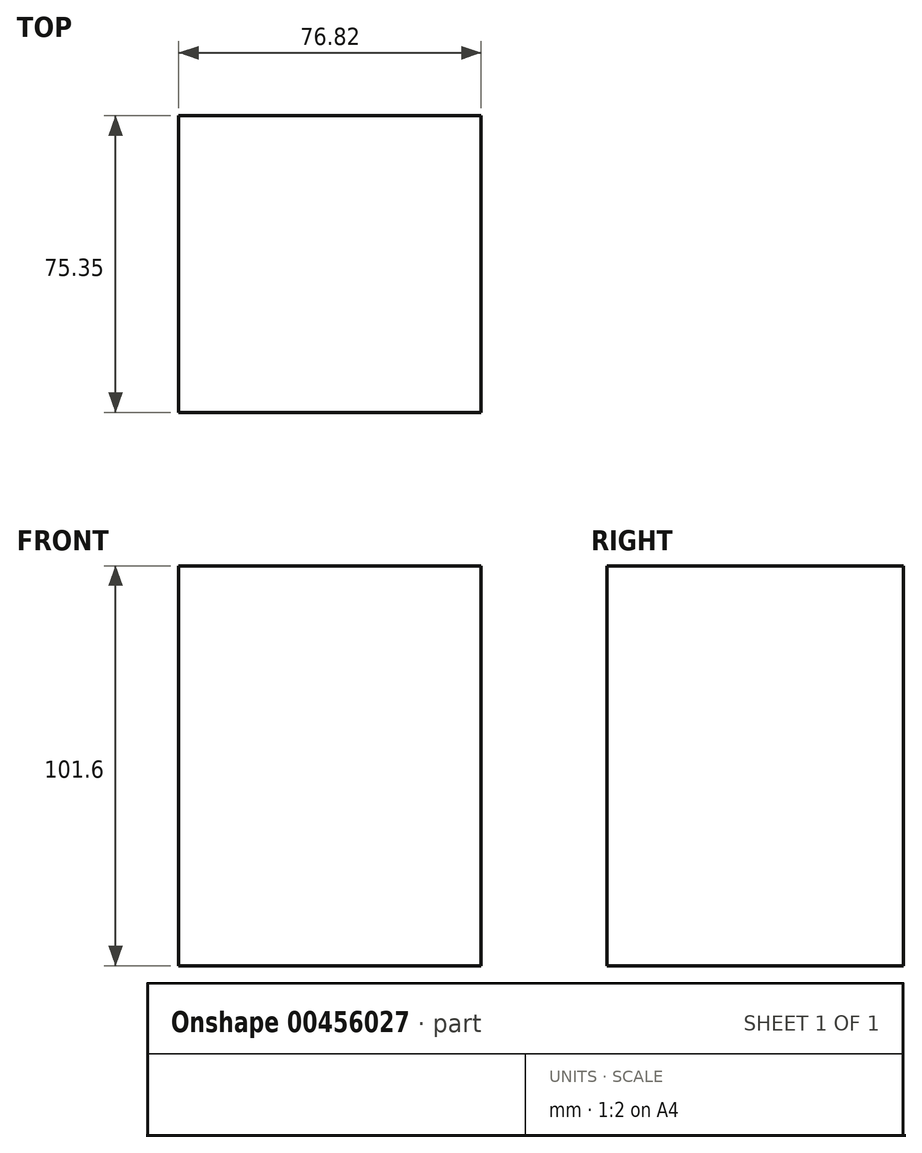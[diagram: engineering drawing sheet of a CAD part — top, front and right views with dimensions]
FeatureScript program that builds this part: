
annotation { "Feature Type Name" : "Feature", "Feature Type Description" : "" }
export const myFeature = defineFeature(function(context is Context, id is Id, definition is map)
    precondition{}
    {
        {
            var Q0;
            Q0=qCreatedBy(makeId("Top.planeOp"),FACE);
            var sketch = newSketch(context, id + "F0", { "sketchPlane" : qUnion([Q0])});
            skLineSegment(sketch, "E0.bottom", {"start": v(0, 0) * mm, "end": v(76.82, 0) * mm});
            skLineSegment(sketch, "E0.top", {"start": v(0, 75.35) * mm, "end": v(76.82, 75.35) * mm});
            skLineSegment(sketch, "E0.left", {"start": v(0, 0) * mm, "end": v(0, 75.35) * mm});
            skLineSegment(sketch, "E0.right", {"start": v(76.82, 0) * mm, "end": v(76.82, 75.35) * mm});
            skSolve(sketch);
        }
        {
            var Q0;
            Q0=makeQuery(id+"F0.imprint","IMPRINT",FACE,{"disambiguationData":[TD([[makeQuery(id+"F0.imprint","IMPRINT",EDGE,{"derivedFrom":sQuery(id+"F0.wireOp",EDGE,"E0.bottom")}),1.0]])]});
            var sketch = newSketch(context, id + "F1", { "sketchPlane" : qUnion([Q0])});
            skLineSegment(sketch, "E1.bottom", {"start": v(39.55, 39.24) * mm, "end": v(75.99, 39.24) * mm});
            skLineSegment(sketch, "E1.top", {"start": v(39.55, 74.91) * mm, "end": v(75.99, 74.91) * mm});
            skLineSegment(sketch, "E1.left", {"start": v(39.55, 39.24) * mm, "end": v(39.55, 74.91) * mm});
            skLineSegment(sketch, "E1.right", {"start": v(75.99, 39.24) * mm, "end": v(75.99, 74.91) * mm});
            skLineSegment(sketch, "E2.top", {"start": v(39.55, 0) * mm, "end": v(75.99, 0) * mm});
            skLineSegment(sketch, "E2.left", {"start": v(39.55, 39.24) * mm, "end": v(39.55, 0) * mm});
            skLineSegment(sketch, "E2.right", {"start": v(75.99, 39.24) * mm, "end": v(75.99, 0) * mm});
            skLineSegment(sketch, "E3.bottom", {"start": v(39.55, 39.24) * mm, "end": v(0, 39.24) * mm});
            skLineSegment(sketch, "E3.top", {"start": v(39.55, 74.91) * mm, "end": v(0, 74.91) * mm});
            skLineSegment(sketch, "E3.right", {"start": v(0, 39.24) * mm, "end": v(0, 74.91) * mm});
            skLineSegment(sketch, "E4.top", {"start": v(39.55, 0) * mm, "end": v(0, 0) * mm});
            skLineSegment(sketch, "E4.right", {"start": v(0, 39.24) * mm, "end": v(0, 0) * mm});
            skSolve(sketch);
        }
        {
            var Q0;
            Q0=makeQuery(id+"F0.imprint","IMPRINT",FACE,{"disambiguationData":[TD([[makeQuery(id+"F0.imprint","IMPRINT",EDGE,{"derivedFrom":sQuery(id+"F0.wireOp",EDGE,"E0.bottom")}),1.0]])]});
            var sketch = newSketch(context, id + "F2", { "sketchPlane" : qUnion([Q0])});
            skLineSegment(sketch, "E5.bottom", {"start": v(0, 75.68) * mm, "end": v(43.37, 75.68) * mm});
            skLineSegment(sketch, "E5.top", {"start": v(0, 35.16) * mm, "end": v(43.37, 35.16) * mm});
            skLineSegment(sketch, "E5.left", {"start": v(0, 75.68) * mm, "end": v(0, 35.16) * mm});
            skLineSegment(sketch, "E5.right", {"start": v(43.37, 75.68) * mm, "end": v(43.37, 35.16) * mm});
            skLineSegment(sketch, "E6.bottom", {"start": v(76.75, 0) * mm, "end": v(35.22, 0) * mm});
            skLineSegment(sketch, "E6.top", {"start": v(76.75, 44.34) * mm, "end": v(35.22, 44.34) * mm});
            skLineSegment(sketch, "E6.left", {"start": v(76.75, 0) * mm, "end": v(76.75, 44.34) * mm});
            skLineSegment(sketch, "E6.right", {"start": v(35.22, 0) * mm, "end": v(35.22, 44.34) * mm});
            skSolve(sketch);
        }
        {
            var Q0;
            Q0=makeQuery(id+"F0.imprint","IMPRINT",FACE,{"disambiguationData":[TD([[makeQuery(id+"F0.imprint","IMPRINT",EDGE,{"derivedFrom":sQuery(id+"F0.wireOp",EDGE,"E0.bottom")}),1.0]])]});
            var sketch = newSketch(context, id + "F3", { "sketchPlane" : qUnion([Q0])});
            skLineSegment(sketch, "E7.bottom", {"start": v(43.12, 75.93) * mm, "end": v(75.99, 75.93) * mm});
            skLineSegment(sketch, "E7.top", {"start": v(43.12, 44.85) * mm, "end": v(75.99, 44.85) * mm});
            skLineSegment(sketch, "E7.left", {"start": v(43.12, 75.93) * mm, "end": v(43.12, 44.85) * mm});
            skLineSegment(sketch, "E7.right", {"start": v(75.99, 75.93) * mm, "end": v(75.99, 44.85) * mm});
            skLineSegment(sketch, "E8.bottom", {"start": v(0, 35.16) * mm, "end": v(34.97, 35.16) * mm});
            skLineSegment(sketch, "E8.top", {"start": v(0, 0) * mm, "end": v(34.97, 0) * mm});
            skLineSegment(sketch, "E8.left", {"start": v(0, 35.16) * mm, "end": v(0, 0) * mm});
            skLineSegment(sketch, "E8.right", {"start": v(34.97, 35.16) * mm, "end": v(34.97, 0) * mm});
            skSolve(sketch);
        }
        {
            var Q0;
            Q0=makeQuery(id+"F0.imprint","IMPRINT",FACE,{"disambiguationData":[TD([[makeQuery(id+"F0.imprint","IMPRINT",EDGE,{"derivedFrom":sQuery(id+"F0.wireOp",EDGE,"E0.bottom")}),1.0]])]});
            extrude(context, id + "F4", {"entities" : qUnion([Q0]), "depth" : 101.6 * mm});
        }
        {
            var Q0;
            {var subQ1=sQuery(id+"F2.wireOp",EDGE,"E6.left");Q0=makeQuery(id+"F2.imprint","IMPRINT",FACE,{"disambiguationData":[TD([[makeQuery(id+"F2.imprint","IMPRINT",EDGE,{"derivedFrom":subQ1}),-1.0]])]});}
            extrude(context, id + "F5", {"entities" : qUnion([Q0]), "operationType" : NewBodyOperationType.REMOVE, "oppositeDirection" : true, "depth" : 101.6 * mm});
        }
        {
            var Q0;
            {var subQ0=sQuery(id+"F3.wireOp",EDGE,"E7.top");Q0=makeQuery(id+"F3.imprint","IMPRINT",FACE,{"disambiguationData":[TD([[makeQuery(id+"F3.imprint","IMPRINT",EDGE,{"derivedFrom":subQ0}),1.0]])]});}
            extrude(context, id + "F6", {"entities" : qUnion([Q0]), "operationType" : NewBodyOperationType.ADD, "depth" : 101.6 * mm});
        }
        {
            var Q0;
            Q0=makeQuery(id+"F1.imprint","IMPRINT",FACE,{"disambiguationData":[TD([[makeQuery(id+"F1.imprint","IMPRINT",EDGE,{"derivedFrom":sQuery(id+"F1.wireOp",EDGE,"E1.top")}),-1.0]])]});
            extrude(context, id + "F7", {"entities" : qUnion([Q0]), "operationType" : NewBodyOperationType.ADD, "depth" : 101.6 * mm});
        }
    });
